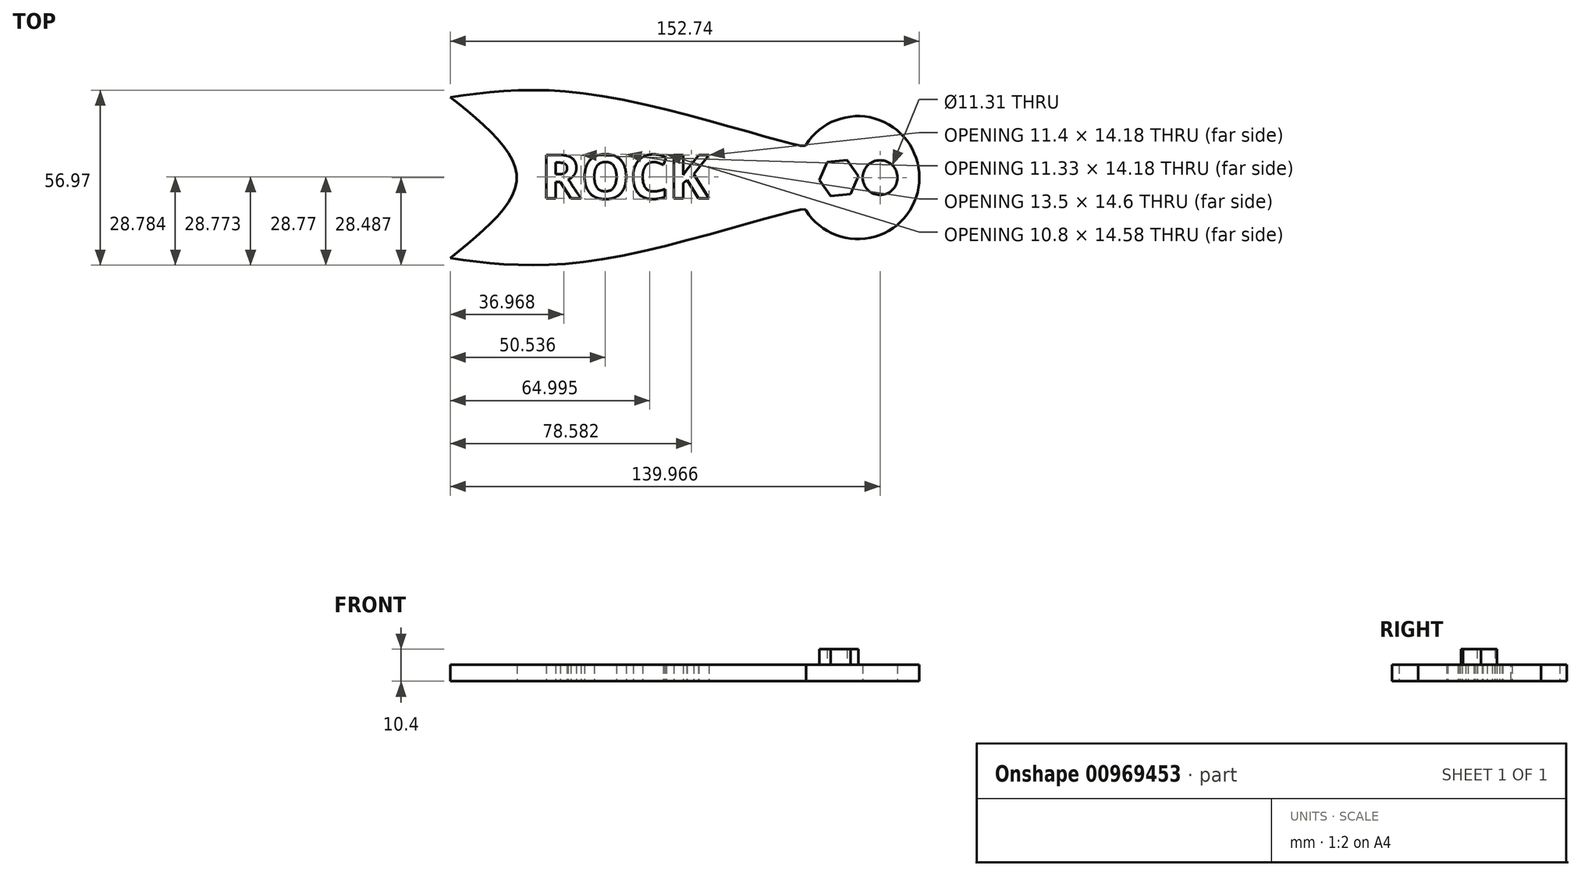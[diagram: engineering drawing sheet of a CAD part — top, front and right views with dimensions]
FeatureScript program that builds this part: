
annotation { "Feature Type Name" : "Feature", "Feature Type Description" : "" }
export const myFeature = defineFeature(function(context is Context, id is Id, definition is map)
    precondition{}
    {
        {
            var Q0;
            Q0=qCreatedBy(makeId("Top.planeOp"),FACE);
            var sketch = newSketch(context, id + "F0", { "sketchPlane" : qUnion([Q0])});
            skFitSpline(sketch, "E0", {"points": [v(-90.84, 33) * mm, v(-39.13, 33) * mm, v(24.65, 17.15) * mm, v(25, 17.5) * mm], "startDerivative": vector(97.6, 13.2) * mm, "endDerivative": vector(2.44, 10.04) * mm});
            skFitSpline(sketch, "E1.MirrorCS", {"points": [v(-90.84, -19.4) * mm, v(-39.13, -19.4) * mm, v(24.65, -3.54) * mm, v(25, -3.88) * mm], "startDerivative": vector(97.6, -13.2) * mm, "endDerivative": vector(2.44, -10.04) * mm});
            skArc(sketch, "E2", {"start": v(25, -3.88) * mm, "mid": v(61.9, 6.8) * mm, "end": v(25, 17.5) * mm});
            skFitSpline(sketch, "E3", {"points": [v(-90.84, 33) * mm, v(-69.12, 6.8) * mm, v(-90.84, -19.4) * mm], "startDerivative": vector(65.16, -52.4) * mm, "endDerivative": vector(-65.16, -52.4) * mm});
            skCircle(sketch, "E4", {"center": v(49.13, 6.8) * mm, "radius": 5.65 * mm});
            skSolve(sketch);
        }
        {
            var Q0;
            Q0=makeQuery(id+"F0.imprint","IMPRINT",FACE,{"disambiguationData":[TD([[makeQuery(id+"F0.imprint","IMPRINT",EDGE,{"derivedFrom":sQuery(id+"F0.wireOp",EDGE,"E0")}),-1.0]])]});
            extrude(context, id + "F1", {"entities" : qUnion([Q0]), "depth" : 5.4 * mm, "offsetDistance" : 25 * mm});
        }
        {
            var Q0;
            Q0=qCreatedBy(makeId("Top.planeOp"),FACE);
            var sketch = newSketch(context, id + "F2", { "sketchPlane" : qUnion([Q0])});
            skText(sketch, "E5", { "text": "ROCK", "fontName": "OpenSans-Bold.ttf"});
            const initialGuessF2  = {"E5": [-0.06132, 0, 1, 0, 0.0143]};
            skSetInitialGuess(sketch, initialGuessF2);
            skSolve(sketch);
        }
        {
            var Q0;
            Q0 = qSketchRegion(id + "F2", true);
            extrude(context, id + "F3", {"entities" : qUnion([Q0]), "operationType" : NewBodyOperationType.REMOVE, "depth" : 43.6 * mm, "offsetDistance" : 25 * mm});
        }
        {
            var Q0;
            Q0=qCreatedBy(makeId("Top.planeOp"),FACE);
            var sketch = newSketch(context, id + "F4", { "sketchPlane" : qUnion([Q0])});
            skCircle(sketch, "E6.cCircle", {"center": v(35.7, 6.62) * mm, "radius": 5.55 * mm, "construction": true});
            skLineSegment(sketch, "E6.0", {"start": v(33.08, 0.77) * mm, "end": v(29.33, 5.97) * mm});
            skLineSegment(sketch, "E6.1", {"start": v(29.33, 5.97) * mm, "end": v(31.95, 11.82) * mm});
            skLineSegment(sketch, "E6.2", {"start": v(31.95, 11.82) * mm, "end": v(38.33, 12.47) * mm});
            skLineSegment(sketch, "E6.3", {"start": v(38.33, 12.47) * mm, "end": v(42.08, 7.27) * mm});
            skLineSegment(sketch, "E6.4", {"start": v(42.08, 7.27) * mm, "end": v(39.46, 1.43) * mm});
            skLineSegment(sketch, "E6.5", {"start": v(39.46, 1.43) * mm, "end": v(33.08, 0.77) * mm});
            skPoint(sketch, "E6.0.midPoint", {"position": v(31.2, 3.37) * mm});
            skSolve(sketch);
        }
        {
            var Q0;
            Q0 = qSketchRegion(id + "F4", true);
            extrude(context, id + "F5", {"entities" : qUnion([Q0]), "operationType" : NewBodyOperationType.ADD, "depth" : 10.4 * mm, "offsetDistance" : 25 * mm});
        }
    });
